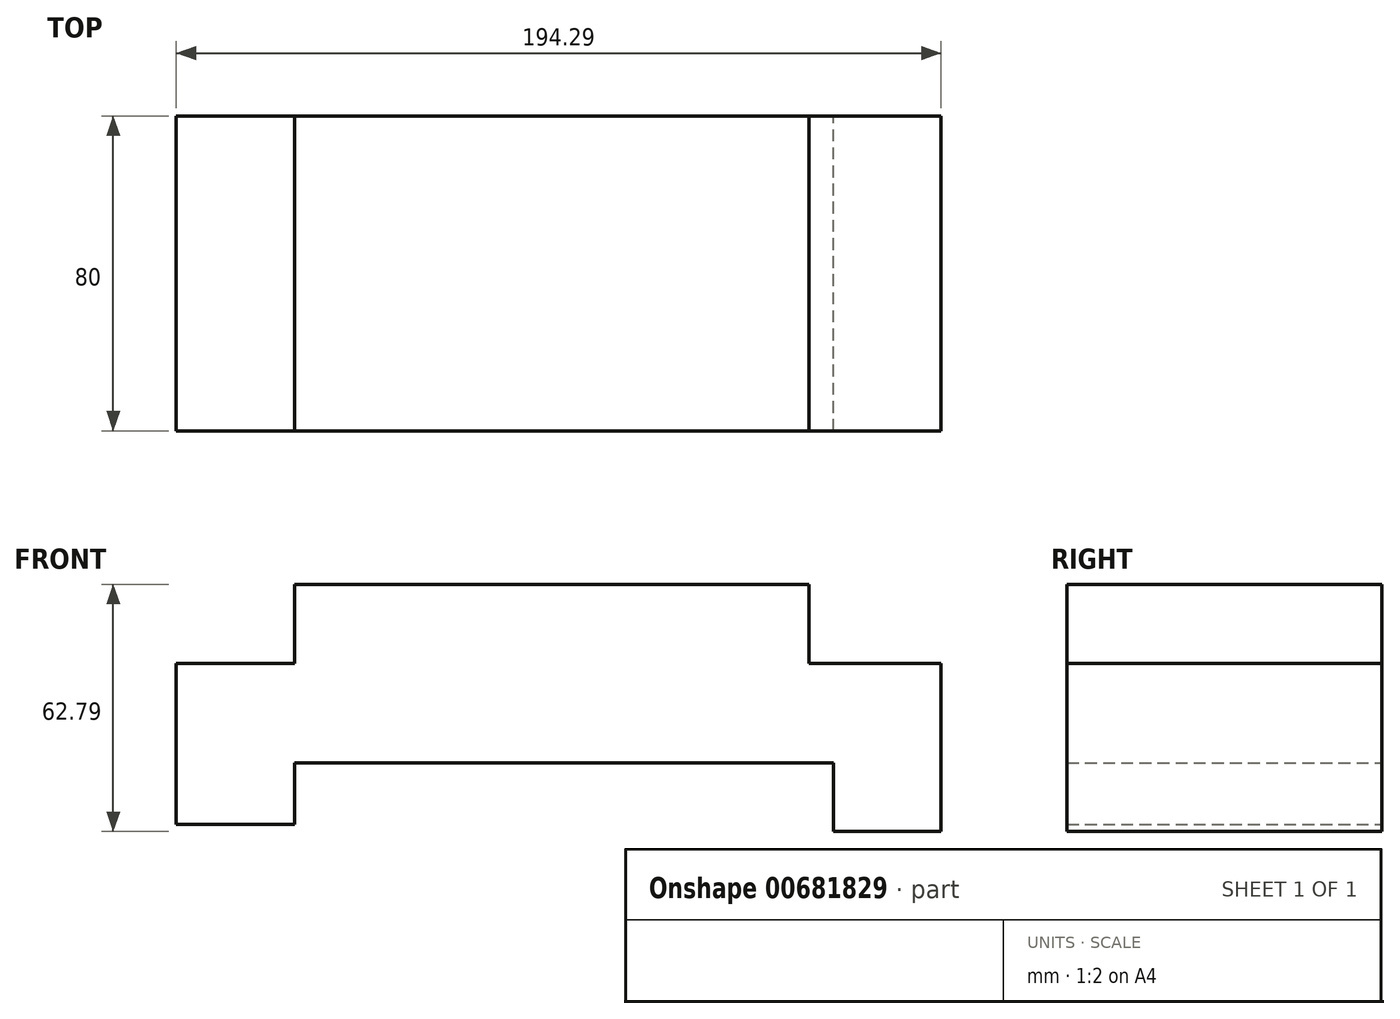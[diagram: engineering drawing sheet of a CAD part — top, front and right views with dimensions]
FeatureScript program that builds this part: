
annotation { "Feature Type Name" : "Feature", "Feature Type Description" : "" }
export const myFeature = defineFeature(function(context is Context, id is Id, definition is map)
    precondition{}
    {
        {
            var Q0;
            Q0=qCreatedBy(makeId("Front.planeOp"),FACE);
            var sketch = newSketch(context, id + "F0", { "sketchPlane" : qUnion([Q0])});
            skLineSegment(sketch, "E0", {"start": v(-79.68, 68.1) * mm, "end": v(51.03, 68.1) * mm});
            skLineSegment(sketch, "E1", {"start": v(51.03, 68.1) * mm, "end": v(51.03, 47.96) * mm});
            skLineSegment(sketch, "E2", {"start": v(51.03, 47.96) * mm, "end": v(84.6, 47.96) * mm});
            skLineSegment(sketch, "E3", {"start": v(84.6, 47.96) * mm, "end": v(84.6, 5.31) * mm});
            skLineSegment(sketch, "E4", {"start": v(84.6, 5.31) * mm, "end": v(57.3, 5.31) * mm});
            skLineSegment(sketch, "E5", {"start": v(57.3, 5.31) * mm, "end": v(57.3, 22.77) * mm});
            skLineSegment(sketch, "E6", {"start": v(57.3, 22.77) * mm, "end": v(-79.68, 22.77) * mm});
            skLineSegment(sketch, "E7", {"start": v(-79.68, 22.77) * mm, "end": v(-79.68, 7.1) * mm});
            skLineSegment(sketch, "E8", {"start": v(-79.68, 7.1) * mm, "end": v(-109.68, 7.1) * mm});
            skLineSegment(sketch, "E9", {"start": v(-109.68, 7.1) * mm, "end": v(-109.68, 47.96) * mm});
            skLineSegment(sketch, "E10", {"start": v(-109.68, 47.96) * mm, "end": v(-79.68, 47.96) * mm});
            skLineSegment(sketch, "E11", {"start": v(-79.68, 47.96) * mm, "end": v(-79.68, 68.1) * mm});
            skSolve(sketch);
        }
        {
            var Q0;
            Q0 = qSketchRegion(id + "F0", true);
            extrude(context, id + "F1", {"entities" : qUnion([Q0]), "depth" : 80 * mm, "offsetDistance" : 25 * mm});
        }
    });
